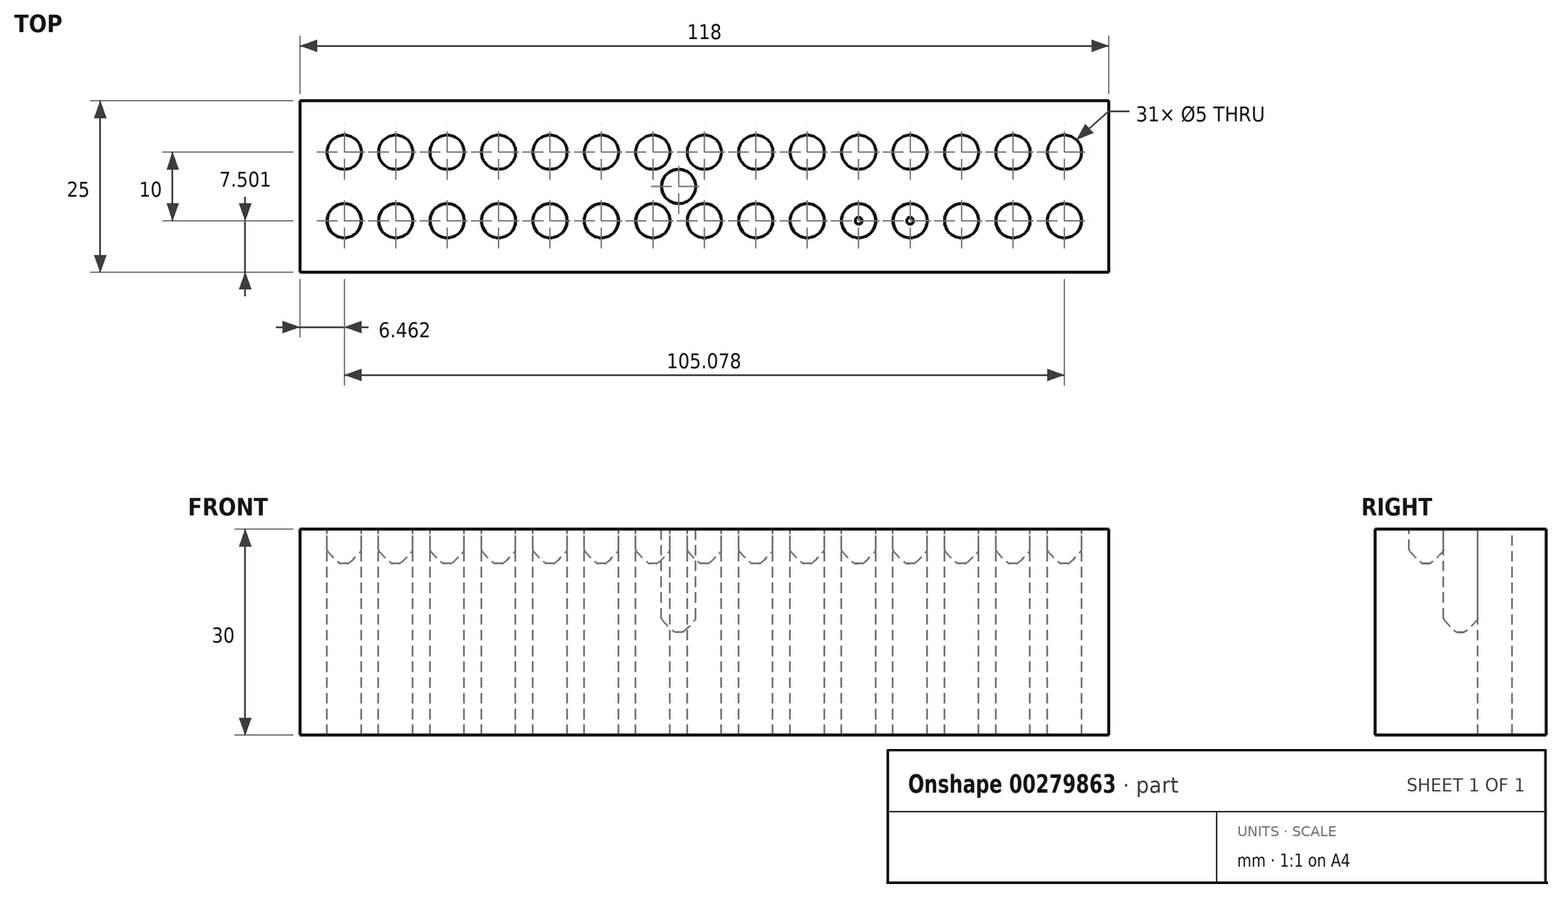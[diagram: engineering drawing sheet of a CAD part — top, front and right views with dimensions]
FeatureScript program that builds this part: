
annotation { "Feature Type Name" : "Feature", "Feature Type Description" : "" }
export const myFeature = defineFeature(function(context is Context, id is Id, definition is map)
    precondition{}
    {
        {
            var Q0;
            Q0=qCreatedBy(makeId("Top.planeOp"),FACE);
            var sketch = newSketch(context, id + "F0", { "sketchPlane" : qUnion([Q0])});
            skLineSegment(sketch, "E0.bottom", {"start": v(-32.4, 15.92) * mm, "end": v(85.6, 15.92) * mm});
            skLineSegment(sketch, "E0.top", {"start": v(-32.4, -9.08) * mm, "end": v(85.6, -9.08) * mm});
            skLineSegment(sketch, "E0.left", {"start": v(-32.4, 15.92) * mm, "end": v(-32.4, -9.08) * mm});
            skLineSegment(sketch, "E0.right", {"start": v(85.6, 15.92) * mm, "end": v(85.6, -9.08) * mm});
            skCircle(sketch, "E1", {"center": v(-25.94, 8.42) * mm, "radius": 2.5 * mm});
            skCircle(sketch, "E2.1.0.0", {"center": v(-18.43, 8.42) * mm, "radius": 2.5 * mm});
            skLineSegment(sketch, "E2.direction1", {"start": v(-25.94, 8.42) * mm, "end": v(-18.43, 8.42) * mm, "construction": true});
            skCircle(sketch, "E3", {"center": v(-25.94, -1.58) * mm, "radius": 2.5 * mm});
            skCircle(sketch, "E4.1.0.0", {"center": v(-18.43, -1.58) * mm, "radius": 2.5 * mm});
            skLineSegment(sketch, "E4.direction1", {"start": v(-25.94, -1.58) * mm, "end": v(-18.43, -1.58) * mm, "construction": true});
            skCircle(sketch, "E5.0.2.0", {"center": v(-10.93, 8.42) * mm, "radius": 2.5 * mm});
            skCircle(sketch, "E5.0.3.0", {"center": v(-3.42, 8.42) * mm, "radius": 2.5 * mm});
            skCircle(sketch, "E5.0.4.0", {"center": v(4.08, 8.42) * mm, "radius": 2.5 * mm});
            skCircle(sketch, "E5.0.5.0", {"center": v(11.59, 8.42) * mm, "radius": 2.5 * mm});
            skCircle(sketch, "E5.0.6.0", {"center": v(19.1, 8.42) * mm, "radius": 2.5 * mm});
            skCircle(sketch, "E5.0.7.0", {"center": v(26.6, 8.42) * mm, "radius": 2.5 * mm});
            skCircle(sketch, "E5.0.8.0", {"center": v(34.1, 8.42) * mm, "radius": 2.5 * mm});
            skCircle(sketch, "E5.0.9.0", {"center": v(41.61, 8.42) * mm, "radius": 2.5 * mm});
            skCircle(sketch, "E5.0.10.0", {"center": v(49.12, 8.42) * mm, "radius": 2.5 * mm});
            skCircle(sketch, "E5.0.11.0", {"center": v(56.62, 8.42) * mm, "radius": 2.5 * mm});
            skCircle(sketch, "E5.0.12.0", {"center": v(64.13, 8.42) * mm, "radius": 2.5 * mm});
            skCircle(sketch, "E5.0.13.0", {"center": v(71.63, 8.42) * mm, "radius": 2.5 * mm});
            skCircle(sketch, "E6.0.2.0", {"center": v(-10.93, -1.58) * mm, "radius": 2.5 * mm});
            skCircle(sketch, "E7.0.3.0", {"center": v(-3.42, -1.58) * mm, "radius": 2.5 * mm});
            skCircle(sketch, "E7.0.4.0", {"center": v(4.08, -1.58) * mm, "radius": 2.5 * mm});
            skCircle(sketch, "E7.0.5.0", {"center": v(11.59, -1.58) * mm, "radius": 2.5 * mm});
            skCircle(sketch, "E7.0.6.0", {"center": v(19.1, -1.58) * mm, "radius": 2.5 * mm});
            skCircle(sketch, "E7.0.7.0", {"center": v(26.6, -1.58) * mm, "radius": 2.5 * mm});
            skCircle(sketch, "E7.0.8.0", {"center": v(34.1, -1.58) * mm, "radius": 2.5 * mm});
            skCircle(sketch, "E7.0.9.0", {"center": v(41.61, -1.58) * mm, "radius": 2.5 * mm});
            skCircle(sketch, "E7.0.10.0", {"center": v(49.12, -1.58) * mm, "radius": 2.5 * mm});
            skCircle(sketch, "E7.0.11.0", {"center": v(56.62, -1.58) * mm, "radius": 2.5 * mm});
            skCircle(sketch, "E7.0.12.0", {"center": v(64.13, -1.58) * mm, "radius": 2.5 * mm});
            skCircle(sketch, "E7.0.13.0", {"center": v(71.63, -1.58) * mm, "radius": 2.5 * mm});
            skLineSegment(sketch, "E8", {"start": v(-28.44, 8.42) * mm, "end": v(-32.4, 8.42) * mm, "construction": true});
            skCircle(sketch, "E9.0.14.0", {"center": v(79.14, -1.58) * mm, "radius": 2.5 * mm});
            skCircle(sketch, "E10.0.14.0", {"center": v(79.14, 8.42) * mm, "radius": 2.5 * mm});
            skLineSegment(sketch, "E11", {"start": v(81.64, 8.42) * mm, "end": v(85.6, 8.42) * mm, "construction": true});
            skCircle(sketch, "E12", {"center": v(22.85, 3.42) * mm, "radius": 2.5 * mm});
            skPoint(sketch, "E12.centerSnap0", {"position": v(-32.4, 3.42) * mm});
            skLineSegment(sketch, "E13", {"start": v(19.1, 8.42) * mm, "end": v(26.6, -1.58) * mm, "construction": true});
            skLineSegment(sketch, "E14", {"start": v(19.1, -1.58) * mm, "end": v(26.6, 8.42) * mm, "construction": true});
            skSolve(sketch);
        }
        {
            var Q0;
            Q0=makeQuery(id+"F0.imprint","IMPRINT",FACE,{"disambiguationData":[TD([[makeQuery(id+"F0.imprint","IMPRINT",EDGE,{"derivedFrom":sQuery(id+"F0.wireOp",EDGE,"E2.2.0.0")}),1.0]])]});
            var Q1;
            Q1=makeQuery(id+"F0.imprint","IMPRINT",FACE,{"disambiguationData":[TD([[makeQuery(id+"F0.imprint","IMPRINT",EDGE,{"derivedFrom":sQuery(id+"F0.wireOp",EDGE,"E2.3.0.0")}),1.0]])]});
            var Q2;
            Q2=makeQuery(id+"F0.imprint","IMPRINT",FACE,{"disambiguationData":[TD([[makeQuery(id+"F0.imprint","IMPRINT",EDGE,{"derivedFrom":sQuery(id+"F0.wireOp",EDGE,"E2.4.0.0")}),1.0]])]});
            var Q3;
            Q3=makeQuery(id+"F0.imprint","IMPRINT",FACE,{"disambiguationData":[TD([[makeQuery(id+"F0.imprint","IMPRINT",EDGE,{"derivedFrom":sQuery(id+"F0.wireOp",EDGE,"E2.5.0.0")}),1.0]])]});
            var Q4;
            Q4=makeQuery(id+"F0.imprint","IMPRINT",FACE,{"disambiguationData":[TD([[makeQuery(id+"F0.imprint","IMPRINT",EDGE,{"derivedFrom":sQuery(id+"F0.wireOp",EDGE,"E2.6.0.0")}),1.0]])]});
            var Q5;
            Q5=makeQuery(id+"F0.imprint","IMPRINT",FACE,{"disambiguationData":[TD([[makeQuery(id+"F0.imprint","IMPRINT",EDGE,{"derivedFrom":sQuery(id+"F0.wireOp",EDGE,"E2.7.0.0")}),1.0]])]});
            var Q6;
            Q6=makeQuery(id+"F0.imprint","IMPRINT",FACE,{"disambiguationData":[TD([[makeQuery(id+"F0.imprint","IMPRINT",EDGE,{"derivedFrom":sQuery(id+"F0.wireOp",EDGE,"E2.8.0.0")}),1.0]])]});
            var Q7;
            Q7=makeQuery(id+"F0.imprint","IMPRINT",FACE,{"disambiguationData":[TD([[makeQuery(id+"F0.imprint","IMPRINT",EDGE,{"derivedFrom":sQuery(id+"F0.wireOp",EDGE,"E2.9.0.0")}),1.0]])]});
            var Q8;
            Q8=makeQuery(id+"F0.imprint","IMPRINT",FACE,{"disambiguationData":[TD([[makeQuery(id+"F0.imprint","IMPRINT",EDGE,{"derivedFrom":sQuery(id+"F0.wireOp",EDGE,"E2.10.0.0")}),1.0]])]});
            var Q9;
            Q9=makeQuery(id+"F0.imprint","IMPRINT",FACE,{"disambiguationData":[TD([[makeQuery(id+"F0.imprint","IMPRINT",EDGE,{"derivedFrom":sQuery(id+"F0.wireOp",EDGE,"E2.11.0.0")}),1.0]])]});
            var Q10;
            Q10=makeQuery(id+"F0.imprint","IMPRINT",FACE,{"disambiguationData":[TD([[makeQuery(id+"F0.imprint","IMPRINT",EDGE,{"derivedFrom":sQuery(id+"F0.wireOp",EDGE,"E2.12.0.0")}),1.0]])]});
            var Q11;
            Q11=makeQuery(id+"F0.imprint","IMPRINT",FACE,{"disambiguationData":[TD([[makeQuery(id+"F0.imprint","IMPRINT",EDGE,{"derivedFrom":sQuery(id+"F0.wireOp",EDGE,"E2.13.0.0")}),1.0]])]});
            var Q12;
            Q12=makeQuery(id+"F0.imprint","IMPRINT",FACE,{"disambiguationData":[TD([[makeQuery(id+"F0.imprint","IMPRINT",EDGE,{"derivedFrom":sQuery(id+"F0.wireOp",EDGE,"E2.14.0.0")}),1.0]])]});
            var Q13;
            Q13=makeQuery(id+"F0.imprint","IMPRINT",FACE,{"disambiguationData":[TD([[makeQuery(id+"F0.imprint","IMPRINT",EDGE,{"derivedFrom":sQuery(id+"F0.wireOp",EDGE,"E4.14.0.0")}),1.0]])]});
            var Q14;
            Q14=makeQuery(id+"F0.imprint","IMPRINT",FACE,{"disambiguationData":[TD([[makeQuery(id+"F0.imprint","IMPRINT",EDGE,{"derivedFrom":sQuery(id+"F0.wireOp",EDGE,"E4.13.0.0")}),1.0]])]});
            var Q15;
            Q15=makeQuery(id+"F0.imprint","IMPRINT",FACE,{"disambiguationData":[TD([[makeQuery(id+"F0.imprint","IMPRINT",EDGE,{"derivedFrom":sQuery(id+"F0.wireOp",EDGE,"E4.12.0.0")}),1.0]])]});
            var Q16;
            Q16=makeQuery(id+"F0.imprint","IMPRINT",FACE,{"disambiguationData":[TD([[makeQuery(id+"F0.imprint","IMPRINT",EDGE,{"derivedFrom":sQuery(id+"F0.wireOp",EDGE,"E4.11.0.0")}),1.0]])]});
            var Q17;
            Q17=makeQuery(id+"F0.imprint","IMPRINT",FACE,{"disambiguationData":[TD([[makeQuery(id+"F0.imprint","IMPRINT",EDGE,{"derivedFrom":sQuery(id+"F0.wireOp",EDGE,"E4.10.0.0")}),1.0]])]});
            var Q18;
            Q18=makeQuery(id+"F0.imprint","IMPRINT",FACE,{"disambiguationData":[TD([[makeQuery(id+"F0.imprint","IMPRINT",EDGE,{"derivedFrom":sQuery(id+"F0.wireOp",EDGE,"E4.9.0.0")}),1.0]])]});
            var Q19;
            Q19=makeQuery(id+"F0.imprint","IMPRINT",FACE,{"disambiguationData":[TD([[makeQuery(id+"F0.imprint","IMPRINT",EDGE,{"derivedFrom":sQuery(id+"F0.wireOp",EDGE,"E4.8.0.0")}),1.0]])]});
            var Q20;
            Q20=makeQuery(id+"F0.imprint","IMPRINT",FACE,{"disambiguationData":[TD([[makeQuery(id+"F0.imprint","IMPRINT",EDGE,{"derivedFrom":sQuery(id+"F0.wireOp",EDGE,"E4.7.0.0")}),1.0]])]});
            var Q21;
            Q21=makeQuery(id+"F0.imprint","IMPRINT",FACE,{"disambiguationData":[TD([[makeQuery(id+"F0.imprint","IMPRINT",EDGE,{"derivedFrom":sQuery(id+"F0.wireOp",EDGE,"E4.6.0.0")}),1.0]])]});
            var Q22;
            Q22=makeQuery(id+"F0.imprint","IMPRINT",FACE,{"disambiguationData":[TD([[makeQuery(id+"F0.imprint","IMPRINT",EDGE,{"derivedFrom":sQuery(id+"F0.wireOp",EDGE,"E4.5.0.0")}),1.0]])]});
            var Q23;
            Q23=makeQuery(id+"F0.imprint","IMPRINT",FACE,{"disambiguationData":[TD([[makeQuery(id+"F0.imprint","IMPRINT",EDGE,{"derivedFrom":sQuery(id+"F0.wireOp",EDGE,"E4.4.0.0")}),1.0]])]});
            var Q24;
            Q24=makeQuery(id+"F0.imprint","IMPRINT",FACE,{"disambiguationData":[TD([[makeQuery(id+"F0.imprint","IMPRINT",EDGE,{"derivedFrom":sQuery(id+"F0.wireOp",EDGE,"E4.3.0.0")}),1.0]])]});
            var Q25;
            Q25=makeQuery(id+"F0.imprint","IMPRINT",FACE,{"disambiguationData":[TD([[makeQuery(id+"F0.imprint","IMPRINT",EDGE,{"derivedFrom":sQuery(id+"F0.wireOp",EDGE,"E4.2.0.0")}),1.0]])]});
            var Q26;
            Q26=makeQuery(id+"F0.imprint","IMPRINT",FACE,{"disambiguationData":[TD([[makeQuery(id+"F0.imprint","IMPRINT",EDGE,{"derivedFrom":sQuery(id+"F0.wireOp",EDGE,"E4.1.0.0")}),1.0]])]});
            var Q27;
            Q27=makeQuery(id+"F0.imprint","IMPRINT",FACE,{"disambiguationData":[TD([[makeQuery(id+"F0.imprint","IMPRINT",EDGE,{"derivedFrom":sQuery(id+"F0.wireOp",EDGE,"E3")}),1.0]])]});
            var Q28;
            Q28=makeQuery(id+"F0.imprint","IMPRINT",FACE,{"disambiguationData":[TD([[makeQuery(id+"F0.imprint","IMPRINT",EDGE,{"derivedFrom":sQuery(id+"F0.wireOp",EDGE,"E6.0.2.0")}),1.0]])]});
            var Q29;
            Q29=makeQuery(id+"F0.imprint","IMPRINT",FACE,{"disambiguationData":[TD([[makeQuery(id+"F0.imprint","IMPRINT",EDGE,{"derivedFrom":sQuery(id+"F0.wireOp",EDGE,"E7.0.3.0")}),1.0]])]});
            var Q30;
            Q30=makeQuery(id+"F0.imprint","IMPRINT",FACE,{"disambiguationData":[TD([[makeQuery(id+"F0.imprint","IMPRINT",EDGE,{"derivedFrom":sQuery(id+"F0.wireOp",EDGE,"E7.0.4.0")}),1.0]])]});
            var Q31;
            Q31=makeQuery(id+"F0.imprint","IMPRINT",FACE,{"disambiguationData":[TD([[makeQuery(id+"F0.imprint","IMPRINT",EDGE,{"derivedFrom":sQuery(id+"F0.wireOp",EDGE,"E7.0.5.0")}),1.0]])]});
            var Q32;
            Q32=makeQuery(id+"F0.imprint","IMPRINT",FACE,{"disambiguationData":[TD([[makeQuery(id+"F0.imprint","IMPRINT",EDGE,{"derivedFrom":sQuery(id+"F0.wireOp",EDGE,"E7.0.6.0")}),1.0]])]});
            var Q33;
            Q33=makeQuery(id+"F0.imprint","IMPRINT",FACE,{"disambiguationData":[TD([[makeQuery(id+"F0.imprint","IMPRINT",EDGE,{"derivedFrom":sQuery(id+"F0.wireOp",EDGE,"E7.0.7.0")}),1.0]])]});
            var Q34;
            Q34=makeQuery(id+"F0.imprint","IMPRINT",FACE,{"disambiguationData":[TD([[makeQuery(id+"F0.imprint","IMPRINT",EDGE,{"derivedFrom":sQuery(id+"F0.wireOp",EDGE,"E7.0.8.0")}),1.0]])]});
            var Q35;
            Q35=makeQuery(id+"F0.imprint","IMPRINT",FACE,{"disambiguationData":[TD([[makeQuery(id+"F0.imprint","IMPRINT",EDGE,{"derivedFrom":sQuery(id+"F0.wireOp",EDGE,"E7.0.9.0")}),1.0]])]});
            var Q36;
            Q36=makeQuery(id+"F0.imprint","IMPRINT",FACE,{"disambiguationData":[TD([[makeQuery(id+"F0.imprint","IMPRINT",EDGE,{"derivedFrom":sQuery(id+"F0.wireOp",EDGE,"E7.0.10.0")}),1.0]])]});
            var Q37;
            Q37=makeQuery(id+"F0.imprint","IMPRINT",FACE,{"disambiguationData":[TD([[makeQuery(id+"F0.imprint","IMPRINT",EDGE,{"derivedFrom":sQuery(id+"F0.wireOp",EDGE,"E7.0.11.0")}),1.0]])]});
            var Q38;
            Q38=makeQuery(id+"F0.imprint","IMPRINT",FACE,{"disambiguationData":[TD([[makeQuery(id+"F0.imprint","IMPRINT",EDGE,{"derivedFrom":sQuery(id+"F0.wireOp",EDGE,"E7.0.12.0")}),1.0]])]});
            var Q39;
            Q39=makeQuery(id+"F0.imprint","IMPRINT",FACE,{"disambiguationData":[TD([[makeQuery(id+"F0.imprint","IMPRINT",EDGE,{"derivedFrom":sQuery(id+"F0.wireOp",EDGE,"E0.bottom")}),-1.0]])]});
            var Q40;
            Q40=makeQuery(id+"F0.imprint","IMPRINT",FACE,{"disambiguationData":[TD([[makeQuery(id+"F0.imprint","IMPRINT",EDGE,{"derivedFrom":sQuery(id+"F0.wireOp",EDGE,"E7.0.13.0")}),1.0]])]});
            var Q41;
            Q41=makeQuery(id+"F0.imprint","IMPRINT",FACE,{"disambiguationData":[TD([[makeQuery(id+"F0.imprint","IMPRINT",EDGE,{"derivedFrom":sQuery(id+"F0.wireOp",EDGE,"E9.0.14.0")}),1.0]])]});
            var Q42;
            Q42=makeQuery(id+"F0.imprint","IMPRINT",FACE,{"disambiguationData":[TD([[makeQuery(id+"F0.imprint","IMPRINT",EDGE,{"derivedFrom":sQuery(id+"F0.wireOp",EDGE,"E12")}),1.0]])]});
            extrude(context, id + "F1", {"entities" : qUnion([Q0, Q1, Q2, Q3, Q4, Q5, Q6, Q7, Q8, Q9, Q10, Q11, Q12, Q13, Q14, Q15, Q16, Q17, Q18, Q19, Q20, Q21, Q22, Q23, Q24, Q25, Q26, Q27, Q28, Q29, Q30, Q31, Q32, Q33, Q34, Q35, Q36, Q37, Q38, Q39, Q40, Q41, Q42]), "oppositeDirection" : true, "depth" : 30 * mm});
        }
        {
            var Q0;
            Q0=makeQuery(id+"F0.imprint","IMPRINT",FACE,{"disambiguationData":[TD([[makeQuery(id+"F0.imprint","IMPRINT",EDGE,{"derivedFrom":sQuery(id+"F0.wireOp",EDGE,"E3")}),1.0]])]});
            var Q1;
            Q1=makeQuery(id+"F0.imprint","IMPRINT",FACE,{"disambiguationData":[TD([[makeQuery(id+"F0.imprint","IMPRINT",EDGE,{"derivedFrom":sQuery(id+"F0.wireOp",EDGE,"E4.1.0.0")}),1.0]])]});
            var Q2;
            Q2=makeQuery(id+"F0.imprint","IMPRINT",FACE,{"disambiguationData":[TD([[makeQuery(id+"F0.imprint","IMPRINT",EDGE,{"derivedFrom":sQuery(id+"F0.wireOp",EDGE,"E6.0.2.0")}),1.0]])]});
            var Q3;
            Q3=makeQuery(id+"F0.imprint","IMPRINT",FACE,{"disambiguationData":[TD([[makeQuery(id+"F0.imprint","IMPRINT",EDGE,{"derivedFrom":sQuery(id+"F0.wireOp",EDGE,"E7.0.3.0")}),1.0]])]});
            var Q4;
            Q4=makeQuery(id+"F0.imprint","IMPRINT",FACE,{"disambiguationData":[TD([[makeQuery(id+"F0.imprint","IMPRINT",EDGE,{"derivedFrom":sQuery(id+"F0.wireOp",EDGE,"E7.0.4.0")}),1.0]])]});
            var Q5;
            Q5=makeQuery(id+"F0.imprint","IMPRINT",FACE,{"disambiguationData":[TD([[makeQuery(id+"F0.imprint","IMPRINT",EDGE,{"derivedFrom":sQuery(id+"F0.wireOp",EDGE,"E7.0.5.0")}),1.0]])]});
            var Q6;
            Q6=makeQuery(id+"F0.imprint","IMPRINT",FACE,{"disambiguationData":[TD([[makeQuery(id+"F0.imprint","IMPRINT",EDGE,{"derivedFrom":sQuery(id+"F0.wireOp",EDGE,"E7.0.6.0")}),1.0]])]});
            var Q7;
            Q7=makeQuery(id+"F0.imprint","IMPRINT",FACE,{"disambiguationData":[TD([[makeQuery(id+"F0.imprint","IMPRINT",EDGE,{"derivedFrom":sQuery(id+"F0.wireOp",EDGE,"E7.0.7.0")}),1.0]])]});
            var Q8;
            Q8=makeQuery(id+"F0.imprint","IMPRINT",FACE,{"disambiguationData":[TD([[makeQuery(id+"F0.imprint","IMPRINT",EDGE,{"derivedFrom":sQuery(id+"F0.wireOp",EDGE,"E7.0.8.0")}),1.0]])]});
            var Q9;
            Q9=makeQuery(id+"F0.imprint","IMPRINT",FACE,{"disambiguationData":[TD([[makeQuery(id+"F0.imprint","IMPRINT",EDGE,{"derivedFrom":sQuery(id+"F0.wireOp",EDGE,"E7.0.9.0")}),1.0]])]});
            var Q10;
            Q10=makeQuery(id+"F0.imprint","IMPRINT",FACE,{"disambiguationData":[TD([[makeQuery(id+"F0.imprint","IMPRINT",EDGE,{"derivedFrom":sQuery(id+"F0.wireOp",EDGE,"E7.0.10.0")}),1.0]])]});
            var Q11;
            Q11=makeQuery(id+"F0.imprint","IMPRINT",FACE,{"disambiguationData":[TD([[makeQuery(id+"F0.imprint","IMPRINT",EDGE,{"derivedFrom":sQuery(id+"F0.wireOp",EDGE,"E7.0.11.0")}),1.0]])]});
            var Q12;
            Q12=makeQuery(id+"F0.imprint","IMPRINT",FACE,{"disambiguationData":[TD([[makeQuery(id+"F0.imprint","IMPRINT",EDGE,{"derivedFrom":sQuery(id+"F0.wireOp",EDGE,"E7.0.12.0")}),1.0]])]});
            var Q13;
            Q13=makeQuery(id+"F0.imprint","IMPRINT",FACE,{"disambiguationData":[TD([[makeQuery(id+"F0.imprint","IMPRINT",EDGE,{"derivedFrom":sQuery(id+"F0.wireOp",EDGE,"E7.0.13.0")}),1.0]])]});
            var Q14;
            Q14=makeQuery(id+"F0.imprint","IMPRINT",FACE,{"disambiguationData":[TD([[makeQuery(id+"F0.imprint","IMPRINT",EDGE,{"derivedFrom":sQuery(id+"F0.wireOp",EDGE,"E9.0.14.0")}),1.0]])]});
            extrude(context, id + "F2", {"entities" : qUnion([Q0, Q1, Q2, Q3, Q4, Q5, Q6, Q7, Q8, Q9, Q10, Q11, Q12, Q13, Q14]), "operationType" : NewBodyOperationType.REMOVE, "oppositeDirection" : true, "depth" : 5 * mm});
        }
        {
            var Q0;
            Q0=makeQuery(id+"F0.imprint","IMPRINT",FACE,{"disambiguationData":[TD([[makeQuery(id+"F0.imprint","IMPRINT",EDGE,{"derivedFrom":sQuery(id+"F0.wireOp",EDGE,"E12")}),1.0]])]});
            extrude(context, id + "F3", {"entities" : qUnion([Q0]), "operationType" : NewBodyOperationType.REMOVE, "oppositeDirection" : true, "depth" : 15 * mm});
        }
        {
            var Q0;
            Q0=makeQuery(id+"F2.boolean.opBoolean","COPY",EDGE,{"derivedFrom":makeQuery(id+"F2.opExtrude","CAP_EDGE",EDGE,{"disambiguationData":[OSD([sQuery(id+"F0.wireOp",EDGE,"E4.1.0.0")])],"isStart":false})});
            var Q1;
            Q1=makeQuery(id+"F2.boolean.opBoolean","COPY",FACE,{"derivedFrom":makeQuery(id+"F2.opExtrude","CAP_FACE",FACE,{"disambiguationData":[OSD([sQuery(id+"F0.wireOp",EDGE,"E3")])],"isStart":false})});
            var Q2;
            Q2=makeQuery(id+"F2.boolean.opBoolean","COPY",EDGE,{"derivedFrom":makeQuery(id+"F2.opExtrude","CAP_EDGE",EDGE,{"disambiguationData":[OSD([sQuery(id+"F0.wireOp",EDGE,"E6.0.2.0")])],"isStart":false})});
            var Q3;
            Q3=makeQuery(id+"F2.boolean.opBoolean","COPY",FACE,{"derivedFrom":makeQuery(id+"F2.opExtrude","CAP_FACE",FACE,{"disambiguationData":[OSD([sQuery(id+"F0.wireOp",EDGE,"E7.0.3.0")])],"isStart":false})});
            var Q4;
            Q4=makeQuery(id+"F2.boolean.opBoolean","COPY",FACE,{"derivedFrom":makeQuery(id+"F2.opExtrude","CAP_FACE",FACE,{"disambiguationData":[OSD([sQuery(id+"F0.wireOp",EDGE,"E7.0.4.0")])],"isStart":false})});
            var Q5;
            Q5=makeQuery(id+"F2.boolean.opBoolean","COPY",EDGE,{"derivedFrom":makeQuery(id+"F2.opExtrude","CAP_EDGE",EDGE,{"disambiguationData":[OSD([sQuery(id+"F0.wireOp",EDGE,"E7.0.5.0")])],"isStart":false})});
            var Q6;
            Q6=makeQuery(id+"F2.boolean.opBoolean","COPY",EDGE,{"derivedFrom":makeQuery(id+"F2.opExtrude","CAP_EDGE",EDGE,{"disambiguationData":[OSD([sQuery(id+"F0.wireOp",EDGE,"E7.0.6.0")])],"isStart":false})});
            var Q7;
            Q7=makeQuery(id+"F2.boolean.opBoolean","COPY",EDGE,{"derivedFrom":makeQuery(id+"F2.opExtrude","CAP_EDGE",EDGE,{"disambiguationData":[OSD([sQuery(id+"F0.wireOp",EDGE,"E7.0.7.0")])],"isStart":false})});
            var Q8;
            Q8=makeQuery(id+"F2.boolean.opBoolean","COPY",EDGE,{"derivedFrom":makeQuery(id+"F2.opExtrude","CAP_EDGE",EDGE,{"disambiguationData":[OSD([sQuery(id+"F0.wireOp",EDGE,"E7.0.8.0")])],"isStart":false})});
            var Q9;
            Q9=makeQuery(id+"F2.boolean.opBoolean","COPY",EDGE,{"derivedFrom":makeQuery(id+"F2.opExtrude","CAP_EDGE",EDGE,{"disambiguationData":[OSD([sQuery(id+"F0.wireOp",EDGE,"E7.0.9.0")])],"isStart":false})});
            var Q10;
            Q10=makeQuery(id+"F2.boolean.opBoolean","COPY",EDGE,{"derivedFrom":makeQuery(id+"F2.opExtrude","CAP_EDGE",EDGE,{"disambiguationData":[OSD([sQuery(id+"F0.wireOp",EDGE,"E7.0.10.0")])],"isStart":false})});
            var Q11;
            Q11=makeQuery(id+"F2.boolean.opBoolean","COPY",EDGE,{"derivedFrom":makeQuery(id+"F2.opExtrude","CAP_EDGE",EDGE,{"disambiguationData":[OSD([sQuery(id+"F0.wireOp",EDGE,"E7.0.11.0")])],"isStart":false})});
            var Q12;
            Q12=makeQuery(id+"F2.boolean.opBoolean","COPY",EDGE,{"derivedFrom":makeQuery(id+"F2.opExtrude","CAP_EDGE",EDGE,{"disambiguationData":[OSD([sQuery(id+"F0.wireOp",EDGE,"E7.0.12.0")])],"isStart":false})});
            var Q13;
            Q13=makeQuery(id+"F2.boolean.opBoolean","COPY",EDGE,{"derivedFrom":makeQuery(id+"F2.opExtrude","CAP_EDGE",EDGE,{"disambiguationData":[OSD([sQuery(id+"F0.wireOp",EDGE,"E7.0.13.0")])],"isStart":false})});
            var Q14;
            Q14=makeQuery(id+"F2.boolean.opBoolean","COPY",FACE,{"derivedFrom":makeQuery(id+"F2.opExtrude","CAP_FACE",FACE,{"disambiguationData":[OSD([sQuery(id+"F0.wireOp",EDGE,"E9.0.14.0")])],"isStart":false})});
            var Q15;
            Q15=makeQuery(id+"F3.boolean.opBoolean","COPY",EDGE,{"derivedFrom":makeQuery(id+"F3.opExtrude","CAP_EDGE",EDGE,{"disambiguationData":[OSD([sQuery(id+"F0.wireOp",EDGE,"E12")])],"isStart":false})});
            fillet(context, id + "F4", {"entities" : qUnion([Q0, Q1, Q2, Q3, Q4, Q5, Q6, Q7, Q8, Q9, Q10, Q11, Q12, Q13, Q14, Q15]), "radius" : 2 * mm, "tangentPropagation" : true, "rho" : 0.1, "crossSection" : FilletCrossSection.CONIC, "allowEdgeOverflow" : false});
        }
    });
